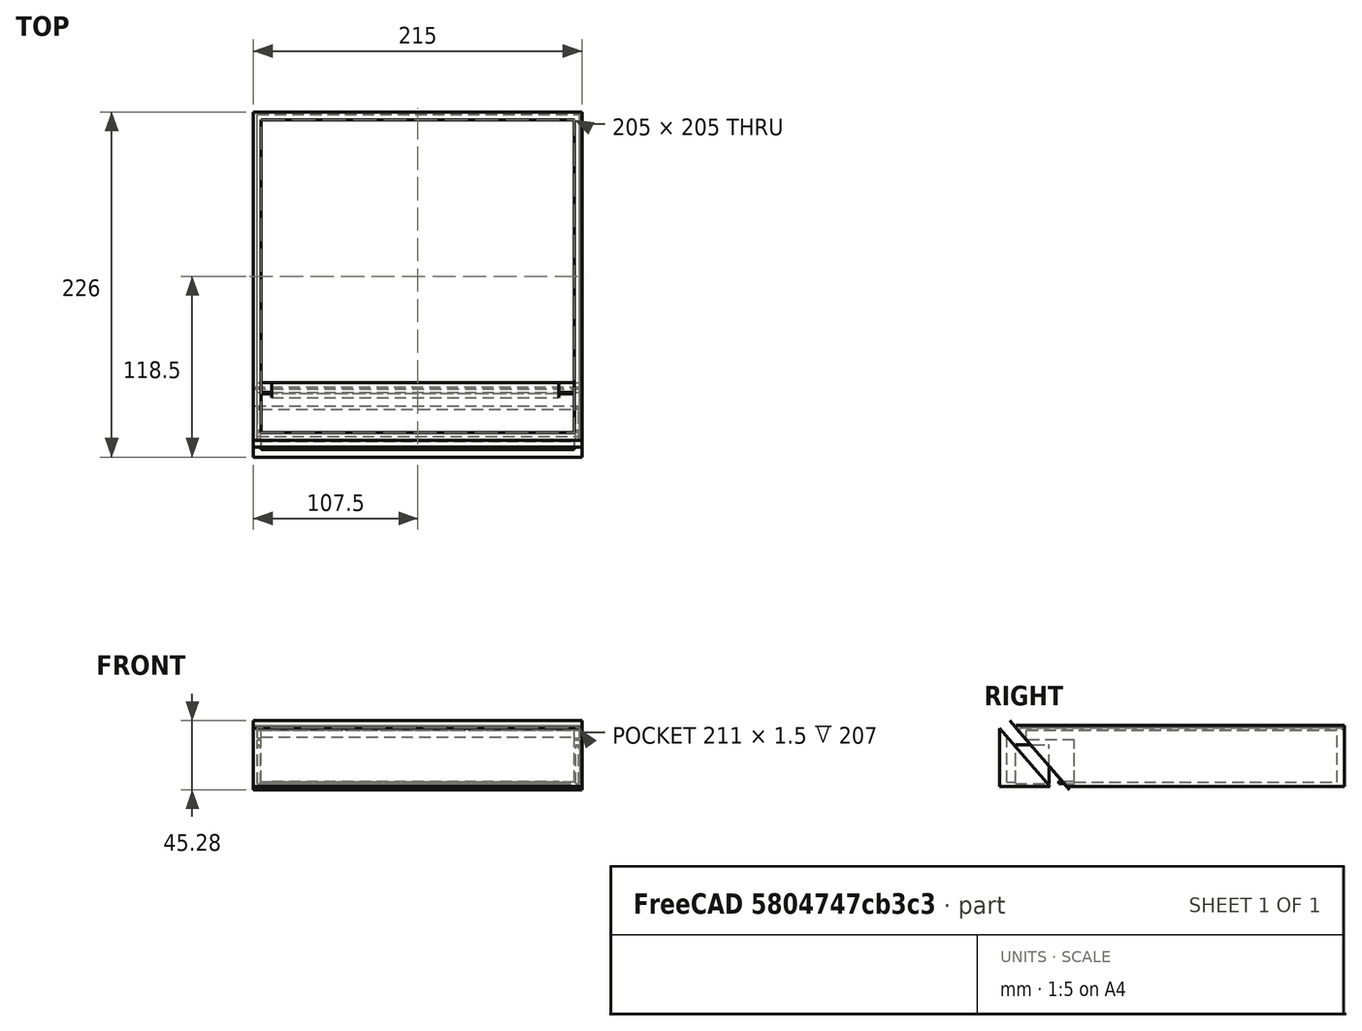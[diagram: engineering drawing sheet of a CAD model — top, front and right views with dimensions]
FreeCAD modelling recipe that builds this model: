
FCSTD DOCUMENT  (FreeCAD 0.18R4 (GitTag))
Label: led16x16BOX
License: All rights reserved
LicenseURL: http://en.wikipedia.org/wiki/All_rights_reserved
objects: Part::Box×10, Part::Cut×5, Part::FeaturePython×4, Part::MultiFuse×2, App::DocumentObjectGroup×1
note: 21 computed .brp shape members not serialized (recipe doc carries the construction recipe); baked Part::Feature solids carry a one-line shape summary decoded from their .brp

FEATURE [Part::Box] Box  label="Cube"
  AttacherType = Attacher::AttachEngine3D
  Height = 40
  Length = 215
  Placement = pos=(-5,-5,0) rot=(0,0,1;0rad)
  Width = 215
FEATURE [Part::Box] Box001  label="Cube001"
  AttacherType = Attacher::AttachEngine3D
  Height = 37
  Length = 205
  Placement = pos=(0,0,3) rot=(0,0,1;0rad)
  Width = 205
FEATURE [Part::Cut] Cut
  Base = -> Box
  Refine = true
  Tool = -> Box001
FEATURE [Part::Box] Box002  label="Cube002"
  AttacherType = Attacher::AttachEngine3D
  Height = 1.5
  Length = 211
  Placement = pos=(-2.5,-2.5,37) rot=(0,0,1;0rad)
  Width = 211
FEATURE [Part::Cut] Cut001
  Base = -> Cut
  Refine = true
  Tool = -> Box002
FEATURE [Part::Box] Box003  label="Cube003"
  AttacherType = Attacher::AttachEngine3D
  Height = 60
  Length = 215
  Placement = pos=(-5,30,-2) rot=(1,0,0;0.715585rad)
  Width = 0.001
FEATURE [Part::FeaturePython] Slice  # WARN: FeaturePython — macro-defined, semantics opaque (R4)
  Base = -> Cut001
  Mode = 1
  Tolerance = 0
  Tools = -> [Box003]
FEATURE [Part::FeaturePython] Slice_child0  label="Door"  # WARN: FeaturePython — macro-defined, semantics opaque (R4)
  Base = -> Slice
  FilterType = 1
  Invert = false
  OverrideMaxVal = 0
  Placement = pos=(0,-11,0) rot=(0,0,1;0rad)
  WindowFrom = 80
  WindowTo = 100
  items = 0
FEATURE [Part::FeaturePython] Slice_child1  label="Slice.1"  # WARN: FeaturePython — macro-defined, semantics opaque (R4)
  Base = -> Slice
  FilterType = 1
  Invert = false
  OverrideMaxVal = 0
  WindowFrom = 80
  WindowTo = 100
  items = 1
FEATURE [Part::FeaturePython] Slice_child2  label="Slice.2"  # WARN: FeaturePython — macro-defined, semantics opaque (R4)
  Base = -> Slice
  FilterType = 1
  Invert = false
  OverrideMaxVal = 0
  WindowFrom = 80
  WindowTo = 100
  items = 2
FEATURE [Part::Box] Box004  label="Cube004"
  AttacherType = Attacher::AttachEngine3D
  Height = 5.5
  Length = 211
  Placement = pos=(-2.5,-5.5,32) rot=(0,0,1;0rad)
  Width = 7
FEATURE [Part::Cut] Cut002  label="Main"
  Base = -> Slice_child2
  Tool = -> Box004
FEATURE [Part::Box] Box005  label="Cube005"
  AttacherType = Attacher::AttachEngine3D
  Height = 28.5
  Length = 211
  Placement = pos=(-2.5,1,2) rot=(0,0,1;0rad)
  Width = 32
FEATURE [Part::Box] Box006  label="Cube006"
  AttacherType = Attacher::AttachEngine3D
  Height = 25.5
  Length = 2
  Placement = pos=(-2.2,-5.5,2) rot=(0,0,1;0rad)
  Width = 22
FEATURE [Part::Box] Box007  label="Cube007"
  AttacherType = Attacher::AttachEngine3D
  Height = 28.5
  Length = 211
  Placement = pos=(-2.5,-5.5,2) rot=(0,0,1;0rad)
  Width = 32
FEATURE [Part::Cut] Cut003
  Base = -> Cut002
  Tool = -> Box005
FEATURE [Part::Cut] Cut004
  Base = -> Slice_child0
  Tool = -> Box007
FEATURE [Part::Box] Box008  label="Cube008"
  AttacherType = Attacher::AttachEngine3D
  Height = 25.5
  Length = 2
  Placement = pos=(206,-5.5,2) rot=(0,0,1;0rad)
  Width = 22
FEATURE [Part::Box] Box009  label="Cube009"
  AttacherType = Attacher::AttachEngine3D
  Height = 1.5
  Length = 188
  Placement = pos=(7,23,2) rot=(0,0,1;0rad)
  Width = 10
FEATURE [Part::MultiFuse] Fusion  label="doorWtabs"
  Refine = true
  Shapes = -> [Box006,Box008,Cut004]
FEATURE [Part::MultiFuse] Fusion001  label="mainWtabs"
  Shapes = -> [Cut003,Box009]
FEATURE [App::DocumentObjectGroup] GrExplode_Slice  label="Exploded Slice"
  Group = -> [Slice_child1,Fusion,Fusion001]
